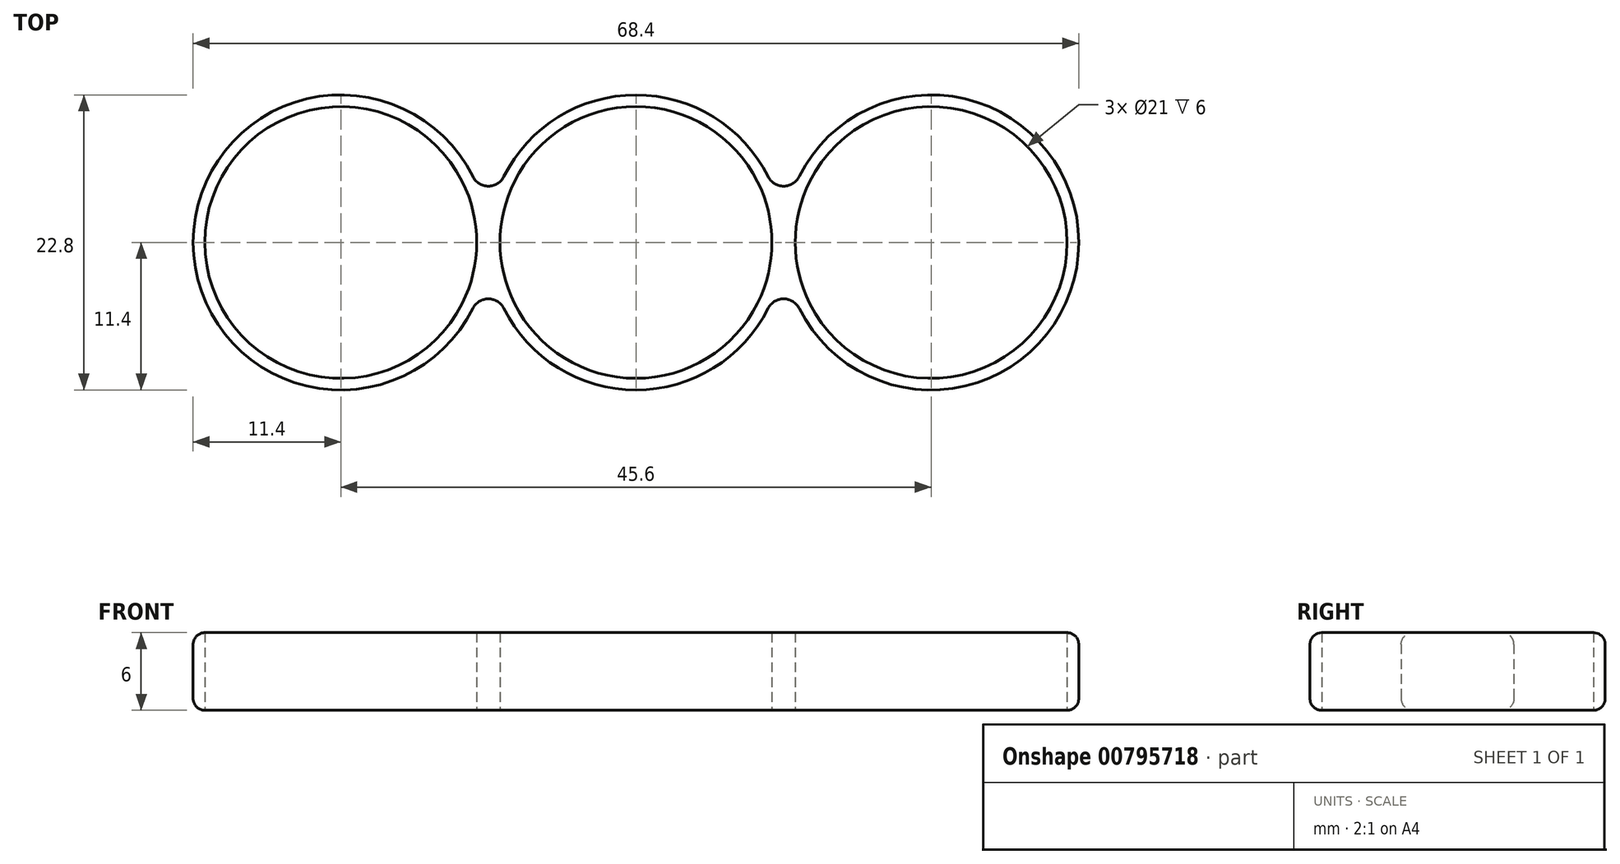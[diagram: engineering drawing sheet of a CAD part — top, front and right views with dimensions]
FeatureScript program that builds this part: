
annotation { "Feature Type Name" : "Feature", "Feature Type Description" : "" }
export const myFeature = defineFeature(function(context is Context, id is Id, definition is map)
    precondition{}
    {
        {
            var Q0;
            Q0=qCreatedBy(makeId("Top.planeOp"),FACE);
            var sketch = newSketch(context, id + "F0", { "sketchPlane" : qUnion([Q0])});
            skCircle(sketch, "E0", {"center": v(0, 0) * mm, "radius": 10.5 * mm});
            skCircle(sketch, "E1", {"center": v(0, 0) * mm, "radius": 11.4 * mm});
            skLineSegment(sketch, "E2", {"start": v(0, 0) * mm, "end": v(22.8, 0) * mm});
            skCircle(sketch, "E3", {"center": v(22.8, 0) * mm, "radius": 11.4 * mm});
            skLineSegment(sketch, "E4", {"start": v(10.5, 0) * mm, "end": v(12.3, 0) * mm});
            skCircle(sketch, "E5", {"center": v(22.8, 0) * mm, "radius": 10.5 * mm});
            skLineSegment(sketch, "E6", {"start": v(0, 0) * mm, "end": v(-22.8, 0) * mm});
            skLineSegment(sketch, "E7", {"start": v(-10.5, 0) * mm, "end": v(-12.3, 0) * mm});
            skCircle(sketch, "E8", {"center": v(-22.8, 0) * mm, "radius": 10.5 * mm});
            skCircle(sketch, "E9", {"center": v(-22.8, 0) * mm, "radius": 11.4 * mm});
            skLineSegment(sketch, "E10", {"start": v(-11.4, 0) * mm, "end": v(-11.4, 5.7) * mm});
            skArc(sketch, "E11", {"start": v(-12.6, 5.1) * mm, "mid": v(-11.4, 4.35) * mm, "end": v(-10.2, 5.1) * mm});
            skLineSegment(sketch, "E12", {"start": v(-11.4, 0) * mm, "end": v(-11.4, -5.7) * mm});
            skLineSegment(sketch, "E13", {"start": v(11.4, 0) * mm, "end": v(11.4, 5.7) * mm});
            skLineSegment(sketch, "E14", {"start": v(11.4, 0) * mm, "end": v(11.4, -5.7) * mm});
            skArc(sketch, "E15", {"start": v(-10.2, -5.1) * mm, "mid": v(-11.4, -4.35) * mm, "end": v(-12.6, -5.1) * mm});
            skArc(sketch, "E16", {"start": v(12.6, -5.1) * mm, "mid": v(11.4, -4.35) * mm, "end": v(10.2, -5.1) * mm});
            skArc(sketch, "E17", {"start": v(10.2, 5.1) * mm, "mid": v(11.4, 4.35) * mm, "end": v(12.6, 5.1) * mm});
            skSolve(sketch);
        }
        {
            var Q0;
            Q0=makeQuery(id+"F0.imprint","IMPRINT",FACE,{"disambiguationData":[TD([[makeQuery(id+"F0.imprint","IMPRINT",EDGE,{"derivedFrom":sQuery(id+"F0.wireOp",EDGE,"E8")}),-1.0]])]});
            var Q1;
            {var subQ1=sQuery(id+"F0.wireOp",EDGE,"E9");var subQ3=sQuery(id+"F0.wireOp",EDGE,"E11");var subQ4=makeQuery(id+"F0.imprint","INTERSECT",VERTEX,{"derivedFrom":[subQ1,subQ3]});Q1=makeQuery(id+"F0.imprint","IMPRINT",FACE,{"disambiguationData":[TD([[makeQuery(id+"F0.imprint","IMPRINT",EDGE,{"disambiguationData":[TD([[subQ4,-1.0]])],"derivedFrom":subQ3}),-1.0]])]});}
            var Q2;
            {var subQ1=sQuery(id+"F0.wireOp",EDGE,"E1");var subQ3=sQuery(id+"F0.wireOp",EDGE,"E11");var subQ4=makeQuery(id+"F0.imprint","INTERSECT",VERTEX,{"derivedFrom":[subQ1,subQ3]});Q2=makeQuery(id+"F0.imprint","IMPRINT",FACE,{"disambiguationData":[TD([[makeQuery(id+"F0.imprint","IMPRINT",EDGE,{"disambiguationData":[TD([[subQ4,1.0]])],"derivedFrom":subQ3}),-1.0]])]});}
            var Q3;
            {var subQ1=sQuery(id+"F0.wireOp",EDGE,"E9");var subQ3=sQuery(id+"F0.wireOp",EDGE,"E15");var subQ4=makeQuery(id+"F0.imprint","INTERSECT",VERTEX,{"derivedFrom":[subQ1,subQ3]});Q3=makeQuery(id+"F0.imprint","IMPRINT",FACE,{"disambiguationData":[TD([[makeQuery(id+"F0.imprint","IMPRINT",EDGE,{"disambiguationData":[TD([[subQ4,1.0]])],"derivedFrom":subQ3}),-1.0]])]});}
            var Q4;
            {var subQ1=sQuery(id+"F0.wireOp",EDGE,"E1");var subQ6=makeQuery(id+"F0.imprint","INTERSECT",VERTEX,{"derivedFrom":[subQ1,sQuery(id+"F0.wireOp",EDGE,"E15")]});Q4=makeQuery(id+"F0.imprint","IMPRINT",FACE,{"disambiguationData":[TD([[makeQuery(id+"F0.imprint","IMPRINT",EDGE,{"disambiguationData":[TD([[subQ6,-1.0]])],"derivedFrom":subQ1}),1.0]])]});}
            var Q5;
            {var subQ1=sQuery(id+"F0.wireOp",EDGE,"E1");var subQ3=sQuery(id+"F0.wireOp",EDGE,"E15");var subQ4=makeQuery(id+"F0.imprint","INTERSECT",VERTEX,{"derivedFrom":[subQ1,subQ3]});Q5=makeQuery(id+"F0.imprint","IMPRINT",FACE,{"disambiguationData":[TD([[makeQuery(id+"F0.imprint","IMPRINT",EDGE,{"disambiguationData":[TD([[subQ4,-1.0]])],"derivedFrom":subQ3}),-1.0]])]});}
            var Q6;
            {var subQ1=sQuery(id+"F0.wireOp",EDGE,"E1");var subQ3=makeQuery(id+"F0.imprint","INTERSECT",VERTEX,{"derivedFrom":[subQ1,sQuery(id+"F0.wireOp",EDGE,"E11")]});Q6=makeQuery(id+"F0.imprint","IMPRINT",FACE,{"disambiguationData":[TD([[makeQuery(id+"F0.imprint","IMPRINT",EDGE,{"disambiguationData":[TD([[subQ3,1.0]])],"derivedFrom":subQ1}),1.0]])]});}
            var Q7;
            {var subQ1=sQuery(id+"F0.wireOp",EDGE,"E3");var subQ3=sQuery(id+"F0.wireOp",EDGE,"E17");var subQ4=makeQuery(id+"F0.imprint","INTERSECT",VERTEX,{"derivedFrom":[subQ1,subQ3]});Q7=makeQuery(id+"F0.imprint","IMPRINT",FACE,{"disambiguationData":[TD([[makeQuery(id+"F0.imprint","IMPRINT",EDGE,{"disambiguationData":[TD([[subQ4,1.0]])],"derivedFrom":subQ3}),-1.0]])]});}
            var Q8;
            {var subQ1=sQuery(id+"F0.wireOp",EDGE,"E1");var subQ3=sQuery(id+"F0.wireOp",EDGE,"E17");var subQ4=makeQuery(id+"F0.imprint","INTERSECT",VERTEX,{"derivedFrom":[subQ1,subQ3]});Q8=makeQuery(id+"F0.imprint","IMPRINT",FACE,{"disambiguationData":[TD([[makeQuery(id+"F0.imprint","IMPRINT",EDGE,{"disambiguationData":[TD([[subQ4,-1.0]])],"derivedFrom":subQ3}),-1.0]])]});}
            var Q9;
            {var subQ1=sQuery(id+"F0.wireOp",EDGE,"E3");var subQ3=sQuery(id+"F0.wireOp",EDGE,"E16");var subQ4=makeQuery(id+"F0.imprint","INTERSECT",VERTEX,{"derivedFrom":[subQ1,subQ3]});Q9=makeQuery(id+"F0.imprint","IMPRINT",FACE,{"disambiguationData":[TD([[makeQuery(id+"F0.imprint","IMPRINT",EDGE,{"disambiguationData":[TD([[subQ4,-1.0]])],"derivedFrom":subQ3}),-1.0]])]});}
            var Q10;
            {var subQ1=sQuery(id+"F0.wireOp",EDGE,"E1");var subQ3=sQuery(id+"F0.wireOp",EDGE,"E16");var subQ4=makeQuery(id+"F0.imprint","INTERSECT",VERTEX,{"derivedFrom":[subQ1,subQ3]});Q10=makeQuery(id+"F0.imprint","IMPRINT",FACE,{"disambiguationData":[TD([[makeQuery(id+"F0.imprint","IMPRINT",EDGE,{"disambiguationData":[TD([[subQ4,1.0]])],"derivedFrom":subQ3}),-1.0]])]});}
            var Q11;
            Q11=makeQuery(id+"F0.imprint","IMPRINT",FACE,{"disambiguationData":[TD([[makeQuery(id+"F0.imprint","IMPRINT",EDGE,{"derivedFrom":sQuery(id+"F0.wireOp",EDGE,"E5")}),-1.0]])]});
            extrude(context, id + "F1", {"entities" : qUnion([Q0, Q1, Q2, Q3, Q4, Q5, Q6, Q7, Q8, Q9, Q10, Q11]), "depth" : 6 * mm, "offsetDistance" : 25 * mm});
        }
        {
            var Q0;
            Q0=makeQuery(id+"F1.opExtrude","CAP_EDGE",EDGE,{"disambiguationData":[OSD([sQuery(id+"F0.wireOp",EDGE,"E9")])],"isStart":false});
            var Q1;
            {var subQ0=sQuery(id+"F0.wireOp",EDGE,"E1");Q1=makeQuery(id+"F1.opExtrude","CAP_EDGE",EDGE,{"disambiguationData":[OSD([subQ0]),TDD([makeQuery(id+"F0.imprint","IMPRINT",EDGE,{"disambiguationData":[TD([[makeQuery(id+"F0.imprint","INTERSECT",VERTEX,{"derivedFrom":[subQ0,sQuery(id+"F0.wireOp",EDGE,"E15")]}),-1.0]])],"derivedFrom":subQ0})])],"isStart":true});}
            fillet(context, id + "F2", {"entities" : qUnion([Q0, Q1]), "radius" : 0.9 * mm, "tangentPropagation" : true, "allowEdgeOverflow" : false});
        }
    });
